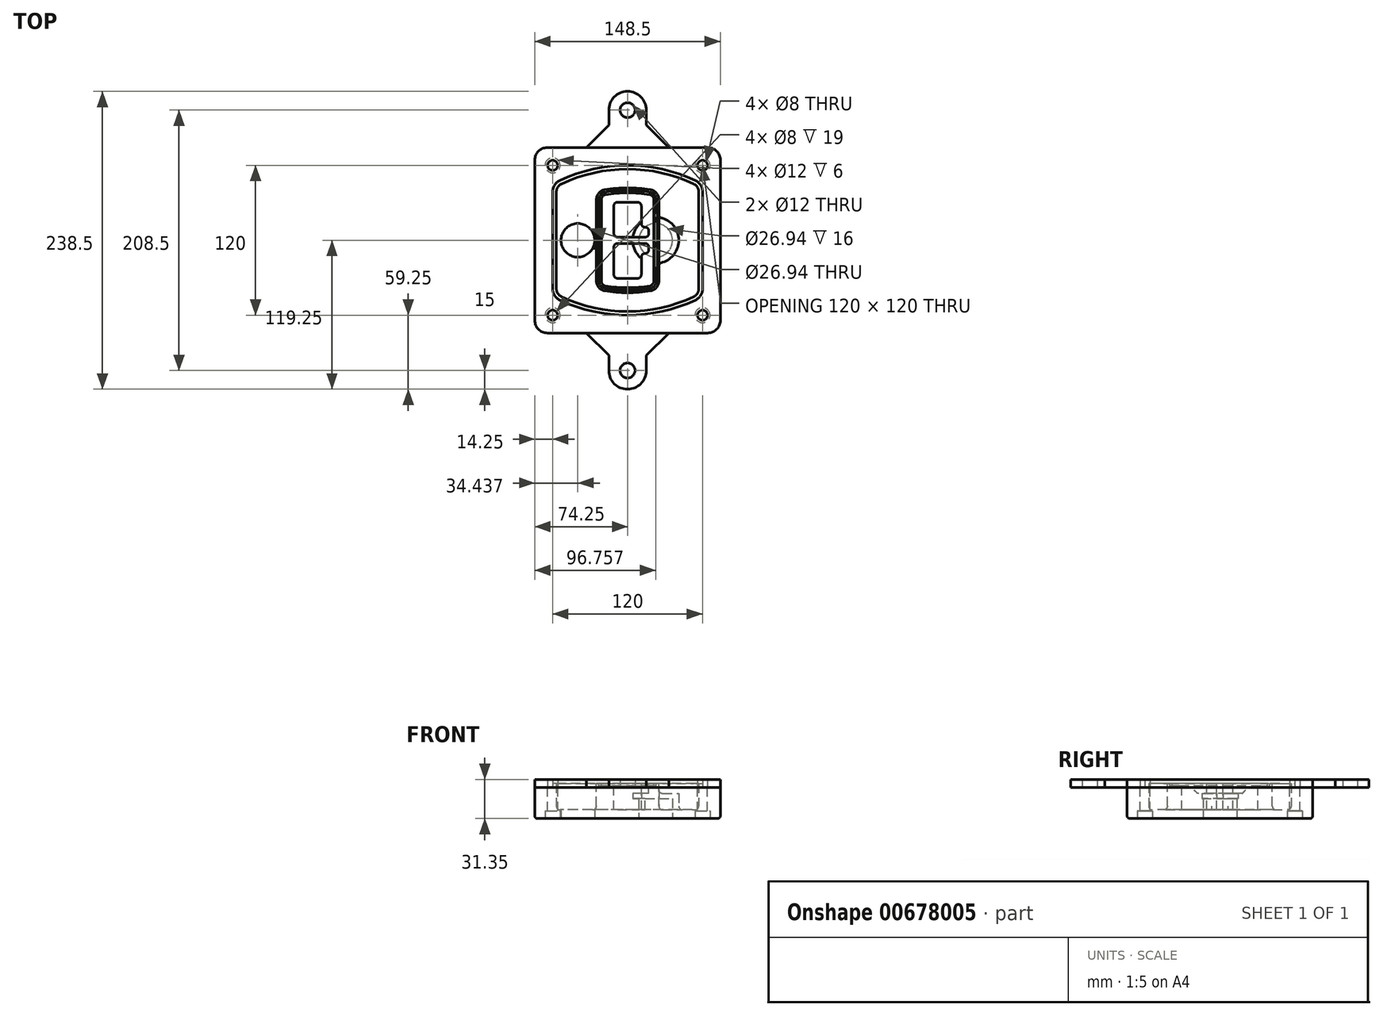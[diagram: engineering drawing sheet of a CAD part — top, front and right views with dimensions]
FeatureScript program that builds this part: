
annotation { "Feature Type Name" : "Feature", "Feature Type Description" : "" }
export const myFeature = defineFeature(function(context is Context, id is Id, definition is map)
    precondition{}
    {
        {
            var Q0;
            Q0=qCreatedBy(makeId("Top.planeOp"),FACE);
            var sketch = newSketch(context, id + "F0", { "sketchPlane" : qUnion([Q0])});
            skPoint(sketch, "E0.rect.middle", {"position": v(0, 0) * mm});
            skLineSegment(sketch, "E1.bottom", {"start": v(-64.25, -74.25) * mm, "end": v(64.25, -74.25) * mm});
            skLineSegment(sketch, "E1.top", {"start": v(-64.25, 74.25) * mm, "end": v(64.25, 74.25) * mm});
            skLineSegment(sketch, "E1.left", {"start": v(-74.25, -64.25) * mm, "end": v(-74.25, 64.25) * mm});
            skLineSegment(sketch, "E1.right", {"start": v(74.25, -64.25) * mm, "end": v(74.25, 64.25) * mm});
            skLineSegment(sketch, "E2", {"start": v(-74.25, 74.25) * mm, "end": v(74.25, -74.25) * mm, "construction": true});
            skLineSegment(sketch, "E3", {"start": v(74.25, 74.25) * mm, "end": v(-74.25, -74.25) * mm, "construction": true});
            skCircle(sketch, "E4", {"center": v(-60, 60) * mm, "radius": 4 * mm});
            skCircle(sketch, "E5", {"center": v(60, 60) * mm, "radius": 4 * mm});
            skCircle(sketch, "E6", {"center": v(60, -60) * mm, "radius": 4 * mm});
            skCircle(sketch, "E7", {"center": v(-60, -60) * mm, "radius": 4 * mm});
            skLineSegment(sketch, "E8", {"start": v(-60, 60) * mm, "end": v(60, 60) * mm, "construction": true});
            skLineSegment(sketch, "E9", {"start": v(60, 60) * mm, "end": v(60, -60) * mm, "construction": true});
            skLineSegment(sketch, "E10", {"start": v(60, -60) * mm, "end": v(-60, -60) * mm, "construction": true});
            skLineSegment(sketch, "E11", {"start": v(-60, -60) * mm, "end": v(-60, 60) * mm, "construction": true});
            skLineSegment(sketch, "E12", {"start": v(-60, 38.83) * mm, "end": v(-60, -38.83) * mm});
            skLineSegment(sketch, "E13", {"start": v(60, 38.83) * mm, "end": v(60, -38.83) * mm});
            skArc(sketch, "E14", {"start": v(54.26, 47.88) * mm, "mid": v(0, 60) * mm, "end": v(-54.26, 47.88) * mm});
            skArc(sketch, "E15", {"start": v(-54.26, -47.88) * mm, "mid": v(0, -60) * mm, "end": v(54.26, -47.88) * mm});
            skLineSegment(sketch, "E16", {"start": v(-60, 0) * mm, "end": v(60, 0) * mm, "construction": true});
            skPoint(sketch, "E17.visualSharp", {"position": v(-60, -45) * mm});
            skArc(sketch, "E17.filletArc", {"start": v(-60, -38.83) * mm, "mid": v(-58.44, -44.2) * mm, "end": v(-54.26, -47.88) * mm});
            skPoint(sketch, "E18.visualSharp", {"position": v(-60, 45) * mm});
            skArc(sketch, "E18.filletArc", {"start": v(-54.26, 47.88) * mm, "mid": v(-58.44, 44.2) * mm, "end": v(-60, 38.83) * mm});
            skPoint(sketch, "E19.visualSharp", {"position": v(60, 45) * mm});
            skArc(sketch, "E19.filletArc", {"start": v(60, 38.83) * mm, "mid": v(58.44, 44.2) * mm, "end": v(54.26, 47.88) * mm});
            skPoint(sketch, "E20.visualSharp", {"position": v(60, -45) * mm});
            skArc(sketch, "E20.filletArc", {"start": v(54.26, -47.88) * mm, "mid": v(58.44, -44.2) * mm, "end": v(60, -38.83) * mm});
            skPoint(sketch, "E21.visualSharp", {"position": v(-74.25, 74.25) * mm});
            skArc(sketch, "E21.filletArc", {"start": v(-64.25, 74.25) * mm, "mid": v(-71.32, 71.32) * mm, "end": v(-74.25, 64.25) * mm});
            skPoint(sketch, "E22.visualSharp", {"position": v(74.25, 74.25) * mm});
            skArc(sketch, "E22.filletArc", {"start": v(74.25, 64.25) * mm, "mid": v(71.32, 71.32) * mm, "end": v(64.25, 74.25) * mm});
            skPoint(sketch, "E23.visualSharp", {"position": v(74.25, -74.25) * mm});
            skArc(sketch, "E23.filletArc", {"start": v(64.25, -74.25) * mm, "mid": v(71.32, -71.32) * mm, "end": v(74.25, -64.25) * mm});
            skPoint(sketch, "E24.visualSharp", {"position": v(-74.25, -74.25) * mm});
            skArc(sketch, "E24.filletArc", {"start": v(-74.25, -64.25) * mm, "mid": v(-71.32, -71.32) * mm, "end": v(-64.25, -74.25) * mm});
            skArc(sketch, "E25.0", {"start": v(57, 38.83) * mm, "mid": v(55.9, 42.58) * mm, "end": v(52.98, 45.17) * mm});
            skLineSegment(sketch, "E25.1", {"start": v(57, 38.83) * mm, "end": v(57, -38.83) * mm});
            skArc(sketch, "E25.2", {"start": v(52.98, -45.17) * mm, "mid": v(55.9, -42.58) * mm, "end": v(57, -38.83) * mm});
            skArc(sketch, "E25.3", {"start": v(-52.98, -45.17) * mm, "mid": v(0, -57) * mm, "end": v(52.98, -45.17) * mm});
            skArc(sketch, "E25.4", {"start": v(-57, -38.83) * mm, "mid": v(-55.9, -42.58) * mm, "end": v(-52.98, -45.17) * mm});
            skArc(sketch, "E25.5", {"start": v(52.98, 45.17) * mm, "mid": v(0, 57) * mm, "end": v(-52.98, 45.17) * mm});
            skLineSegment(sketch, "E25.6", {"start": v(-57, 38.83) * mm, "end": v(-57, -38.83) * mm});
            skArc(sketch, "E25.7", {"start": v(-52.98, 45.17) * mm, "mid": v(-55.9, 42.58) * mm, "end": v(-57, 38.83) * mm});
            skArc(sketch, "E26.0", {"start": v(-55.96, 51.5) * mm, "mid": v(-61.82, 46.33) * mm, "end": v(-64, 38.83) * mm});
            skArc(sketch, "E26.1", {"start": v(55.96, 51.5) * mm, "mid": v(0, 64) * mm, "end": v(-55.96, 51.5) * mm});
            skArc(sketch, "E26.2", {"start": v(64, 38.83) * mm, "mid": v(61.82, 46.33) * mm, "end": v(55.96, 51.5) * mm});
            skLineSegment(sketch, "E26.3", {"start": v(64, 38.83) * mm, "end": v(64, -38.83) * mm});
            skArc(sketch, "E26.4", {"start": v(55.96, -51.5) * mm, "mid": v(61.82, -46.33) * mm, "end": v(64, -38.83) * mm});
            skLineSegment(sketch, "E26.5", {"start": v(-64, 38.83) * mm, "end": v(-64, -38.83) * mm});
            skArc(sketch, "E26.6", {"start": v(-55.96, -51.5) * mm, "mid": v(0, -64) * mm, "end": v(55.96, -51.5) * mm});
            skArc(sketch, "E26.7", {"start": v(-64, -38.83) * mm, "mid": v(-61.82, -46.33) * mm, "end": v(-55.96, -51.5) * mm});
            skSolve(sketch);
        }
        {
            var Q0;
            Q0=makeQuery(id+"F0.imprint","IMPRINT",FACE,{"disambiguationData":[TD([[makeQuery(id+"F0.imprint","IMPRINT",EDGE,{"derivedFrom":sQuery(id+"F0.wireOp",EDGE,"E1.bottom")}),1.0]])]});
            var Q1;
            Q1=makeQuery(id+"F0.imprint","IMPRINT",FACE,{"disambiguationData":[TD([[makeQuery(id+"F0.imprint","IMPRINT",EDGE,{"derivedFrom":sQuery(id+"F0.wireOp",EDGE,"E12")}),1.0]])]});
            var Q2;
            Q2=makeQuery(id+"F0.imprint","IMPRINT",FACE,{"disambiguationData":[TD([[makeQuery(id+"F0.imprint","IMPRINT",EDGE,{"derivedFrom":sQuery(id+"F0.wireOp",EDGE,"E25.0")}),1.0]])]});
            var Q3;
            Q3=makeQuery(id+"F0.imprint","IMPRINT",FACE,{"disambiguationData":[TD([[makeQuery(id+"F0.imprint","IMPRINT",EDGE,{"derivedFrom":sQuery(id+"F0.wireOp",EDGE,"E12")}),-1.0]])]});
            extrude(context, id + "F1", {"entities" : qUnion([Q0, Q1, Q2, Q3]), "oppositeDirection" : true, "depth" : 25 * mm});
        }
        {
            var Q0;
            Q0=makeQuery(id+"F0.imprint","IMPRINT",FACE,{"disambiguationData":[TD([[makeQuery(id+"F0.imprint","IMPRINT",EDGE,{"derivedFrom":sQuery(id+"F0.wireOp",EDGE,"E12")}),1.0]])]});
            extrude(context, id + "F2", {"entities" : qUnion([Q0]), "operationType" : NewBodyOperationType.ADD, "depth" : 3 * mm});
        }
        {
            var Q0;
            Q0=makeQuery(id+"F0.imprint","IMPRINT",FACE,{"disambiguationData":[TD([[makeQuery(id+"F0.imprint","IMPRINT",EDGE,{"derivedFrom":sQuery(id+"F0.wireOp",EDGE,"E25.0")}),1.0]])]});
            extrude(context, id + "F3", {"entities" : qUnion([Q0]), "operationType" : NewBodyOperationType.REMOVE, "oppositeDirection" : true, "depth" : 18 * mm});
        }
        {
            var Q0;
            Q0=makeQuery(id+"F2.opExtrude","CAP_FACE",FACE,{"disambiguationData":[OSD([sQuery(id+"F0.wireOp",EDGE,"E12"),sQuery(id+"F0.wireOp",EDGE,"E13"),sQuery(id+"F0.wireOp",EDGE,"E14"),sQuery(id+"F0.wireOp",EDGE,"E15"),sQuery(id+"F0.wireOp",EDGE,"E17.filletArc"),sQuery(id+"F0.wireOp",EDGE,"E18.filletArc"),sQuery(id+"F0.wireOp",EDGE,"E19.filletArc"),sQuery(id+"F0.wireOp",EDGE,"E20.filletArc"),sQuery(id+"F0.wireOp",EDGE,"E25.0"),sQuery(id+"F0.wireOp",EDGE,"E25.1"),sQuery(id+"F0.wireOp",EDGE,"E25.2"),sQuery(id+"F0.wireOp",EDGE,"E25.3"),sQuery(id+"F0.wireOp",EDGE,"E25.4"),sQuery(id+"F0.wireOp",EDGE,"E25.5"),sQuery(id+"F0.wireOp",EDGE,"E25.6"),sQuery(id+"F0.wireOp",EDGE,"E25.7")])],"isStart":false});
            var sketch = newSketch(context, id + "F4", { "sketchPlane" : qUnion([Q0])});
            skArc(sketch, "E27.0", {"start": v(-18.34, -40.45) * mm, "mid": v(0, -42) * mm, "end": v(18.34, -40.45) * mm});
            skArc(sketch, "E28.0", {"start": v(18.34, 40.45) * mm, "mid": v(0, 42) * mm, "end": v(-18.34, 40.45) * mm});
            skLineSegment(sketch, "E29", {"start": v(-25, 32.57) * mm, "end": v(-25, -32.57) * mm});
            skLineSegment(sketch, "E30", {"start": v(25, 32.57) * mm, "end": v(25, -32.57) * mm});
            skLineSegment(sketch, "E31", {"start": v(-25, 39.1) * mm, "end": v(25, 39.1) * mm, "construction": true});
            skLineSegment(sketch, "E32", {"start": v(-25, -39.1) * mm, "end": v(25, -39.1) * mm, "construction": true});
            skPoint(sketch, "E33.visualSharp", {"position": v(-25, 39.1) * mm});
            skArc(sketch, "E33.filletArc", {"start": v(-18.34, 40.45) * mm, "mid": v(-23.11, 37.73) * mm, "end": v(-25, 32.57) * mm});
            skPoint(sketch, "E34.visualSharp", {"position": v(25, 39.1) * mm});
            skArc(sketch, "E34.filletArc", {"start": v(25, 32.57) * mm, "mid": v(23.11, 37.73) * mm, "end": v(18.34, 40.45) * mm});
            skPoint(sketch, "E35.visualSharp", {"position": v(25, -39.1) * mm});
            skArc(sketch, "E35.filletArc", {"start": v(18.34, -40.45) * mm, "mid": v(23.11, -37.73) * mm, "end": v(25, -32.57) * mm});
            skPoint(sketch, "E36.visualSharp", {"position": v(-25, -39.1) * mm});
            skArc(sketch, "E36.filletArc", {"start": v(-25, -32.57) * mm, "mid": v(-23.11, -37.73) * mm, "end": v(-18.34, -40.45) * mm});
            skArc(sketch, "E37.0", {"start": v(52.98, 45.17) * mm, "mid": v(0, 57) * mm, "end": v(-52.98, 45.17) * mm});
            skArc(sketch, "E37.1", {"start": v(-52.98, 45.17) * mm, "mid": v(-55.9, 42.58) * mm, "end": v(-57, 38.83) * mm});
            skLineSegment(sketch, "E37.2", {"start": v(-57, 38.83) * mm, "end": v(-57, -38.83) * mm});
            skArc(sketch, "E37.3", {"start": v(-57, -38.83) * mm, "mid": v(-55.9, -42.58) * mm, "end": v(-52.98, -45.17) * mm});
            skArc(sketch, "E37.4", {"start": v(-52.98, -45.17) * mm, "mid": v(0, -57) * mm, "end": v(52.98, -45.17) * mm});
            skArc(sketch, "E37.5", {"start": v(52.98, -45.17) * mm, "mid": v(55.9, -42.58) * mm, "end": v(57, -38.83) * mm});
            skLineSegment(sketch, "E37.6", {"start": v(57, 38.83) * mm, "end": v(57, -38.83) * mm});
            skArc(sketch, "E37.7", {"start": v(57, 38.83) * mm, "mid": v(55.9, 42.58) * mm, "end": v(52.98, 45.17) * mm});
            skLineSegment(sketch, "E38.0", {"start": v(23, 32.57) * mm, "end": v(23, -32.57) * mm});
            skArc(sketch, "E38.1", {"start": v(18, -38.48) * mm, "mid": v(21.58, -36.44) * mm, "end": v(23, -32.57) * mm});
            skArc(sketch, "E38.2", {"start": v(-18, -38.48) * mm, "mid": v(0, -40) * mm, "end": v(18, -38.48) * mm});
            skArc(sketch, "E38.3", {"start": v(-23, -32.57) * mm, "mid": v(-21.58, -36.44) * mm, "end": v(-18, -38.48) * mm});
            skLineSegment(sketch, "E38.4", {"start": v(-23, 32.57) * mm, "end": v(-23, -32.57) * mm});
            skArc(sketch, "E38.5", {"start": v(23, 32.57) * mm, "mid": v(21.58, 36.44) * mm, "end": v(18, 38.48) * mm});
            skArc(sketch, "E38.6", {"start": v(-18, 38.48) * mm, "mid": v(-21.58, 36.44) * mm, "end": v(-23, 32.57) * mm});
            skArc(sketch, "E38.7", {"start": v(18, 38.48) * mm, "mid": v(0, 40) * mm, "end": v(-18, 38.48) * mm});
            skArc(sketch, "E39.0", {"start": v(21, 32.57) * mm, "mid": v(20.06, 35.15) * mm, "end": v(17.67, 36.5) * mm});
            skLineSegment(sketch, "E39.1", {"start": v(21, 32.57) * mm, "end": v(21, -32.57) * mm});
            skArc(sketch, "E39.2", {"start": v(17.67, -36.5) * mm, "mid": v(20.06, -35.15) * mm, "end": v(21, -32.57) * mm});
            skArc(sketch, "E39.3", {"start": v(-17.67, -36.5) * mm, "mid": v(0, -38) * mm, "end": v(17.67, -36.5) * mm});
            skArc(sketch, "E39.4", {"start": v(-21, -32.57) * mm, "mid": v(-20.06, -35.15) * mm, "end": v(-17.67, -36.5) * mm});
            skArc(sketch, "E39.5", {"start": v(17.67, 36.5) * mm, "mid": v(0, 38) * mm, "end": v(-17.67, 36.5) * mm});
            skLineSegment(sketch, "E39.6", {"start": v(-21, 32.57) * mm, "end": v(-21, -32.57) * mm});
            skArc(sketch, "E39.7", {"start": v(-17.67, 36.5) * mm, "mid": v(-20.06, 35.15) * mm, "end": v(-21, 32.57) * mm});
            skLineSegment(sketch, "E40", {"start": v(-25, 0) * mm, "end": v(25, 0) * mm, "construction": true});
            skLineSegment(sketch, "E41", {"start": v(-11, 5.5) * mm, "end": v(-11, 27.5) * mm});
            skLineSegment(sketch, "E42", {"start": v(-8, 30.5) * mm, "end": v(8, 30.5) * mm});
            skLineSegment(sketch, "E43", {"start": v(11, 27.5) * mm, "end": v(11, 13.5) * mm});
            skLineSegment(sketch, "E44", {"start": v(14, 10.5) * mm, "end": v(14, 10.5) * mm});
            skLineSegment(sketch, "E45", {"start": v(17, 7.5) * mm, "end": v(17, 5.5) * mm});
            skLineSegment(sketch, "E46", {"start": v(14, 2.5) * mm, "end": v(-8, 2.5) * mm});
            skPoint(sketch, "E47.visualSharp", {"position": v(-11, 30.5) * mm});
            skArc(sketch, "E47.filletArc", {"start": v(-8, 30.5) * mm, "mid": v(-10.12, 29.62) * mm, "end": v(-11, 27.5) * mm});
            skPoint(sketch, "E48.visualSharp", {"position": v(11, 30.5) * mm});
            skArc(sketch, "E48.filletArc", {"start": v(11, 27.5) * mm, "mid": v(10.12, 29.62) * mm, "end": v(8, 30.5) * mm});
            skPoint(sketch, "E49.visualSharp", {"position": v(11, 10.5) * mm});
            skArc(sketch, "E49.filletArc", {"start": v(11, 13.5) * mm, "mid": v(11.88, 11.38) * mm, "end": v(14, 10.5) * mm});
            skPoint(sketch, "E50.visualSharp", {"position": v(17, 10.5) * mm});
            skArc(sketch, "E50.filletArc", {"start": v(17, 7.5) * mm, "mid": v(16.12, 9.62) * mm, "end": v(14, 10.5) * mm});
            skPoint(sketch, "E51.visualSharp", {"position": v(17, 2.5) * mm});
            skArc(sketch, "E51.filletArc", {"start": v(14, 2.5) * mm, "mid": v(16.12, 3.38) * mm, "end": v(17, 5.5) * mm});
            skPoint(sketch, "E52.visualSharp", {"position": v(-11, 2.5) * mm});
            skArc(sketch, "E52.filletArc", {"start": v(-11, 5.5) * mm, "mid": v(-10.12, 3.38) * mm, "end": v(-8, 2.5) * mm});
            skLineSegment(sketch, "E53.0.MirrorCS", {"start": v(14, -2.5) * mm, "end": v(-8, -2.5) * mm});
            skArc(sketch, "E54.0.MirrorCS", {"start": v(-11, -5.5) * mm, "mid": v(-10.12, -3.38) * mm, "end": v(-8, -2.5) * mm});
            skLineSegment(sketch, "E55.0.MirrorCS", {"start": v(-11, -5.5) * mm, "end": v(-11, -27.5) * mm});
            skArc(sketch, "E56.0.MirrorCS", {"start": v(-8, -30.5) * mm, "mid": v(-10.12, -29.62) * mm, "end": v(-11, -27.5) * mm});
            skLineSegment(sketch, "E57.0.MirrorCS", {"start": v(-8, -30.5) * mm, "end": v(8, -30.5) * mm});
            skArc(sketch, "E58.0.MirrorCS", {"start": v(11, -27.5) * mm, "mid": v(10.12, -29.62) * mm, "end": v(8, -30.5) * mm});
            skLineSegment(sketch, "E59.0.MirrorCS", {"start": v(11, -27.5) * mm, "end": v(11, -13.5) * mm});
            skArc(sketch, "E60.0.MirrorCS", {"start": v(11, -13.5) * mm, "mid": v(11.88, -11.38) * mm, "end": v(14, -10.5) * mm});
            skArc(sketch, "E61.0.MirrorCS", {"start": v(17, -7.5) * mm, "mid": v(16.12, -9.62) * mm, "end": v(14, -10.5) * mm});
            skLineSegment(sketch, "E62.0.MirrorCS", {"start": v(17, -7.5) * mm, "end": v(17, -5.5) * mm});
            skArc(sketch, "E63.0.MirrorCS", {"start": v(14, -2.5) * mm, "mid": v(16.12, -3.38) * mm, "end": v(17, -5.5) * mm});
            skSolve(sketch);
        }
        {
            var Q0;
            Q0=makeQuery(id+"F4.imprint","IMPRINT",FACE,{"disambiguationData":[TD([[makeQuery(id+"F4.imprint","IMPRINT",EDGE,{"derivedFrom":sQuery(id+"F4.wireOp",EDGE,"E27.0")}),1.0]])]});
            var Q1;
            Q1=makeQuery(id+"F4.imprint","IMPRINT",FACE,{"disambiguationData":[TD([[makeQuery(id+"F4.imprint","IMPRINT",EDGE,{"derivedFrom":sQuery(id+"F4.wireOp",EDGE,"E38.0")}),-1.0]])]});
            var Q2;
            Q2=makeQuery(id+"F4.imprint","IMPRINT",FACE,{"disambiguationData":[TD([[makeQuery(id+"F4.imprint","IMPRINT",EDGE,{"derivedFrom":sQuery(id+"F4.wireOp",EDGE,"E39.0")}),1.0]])]});
            extrude(context, id + "F5", {"entities" : qUnion([Q0, Q1, Q2]), "operationType" : NewBodyOperationType.ADD, "endBound" : BoundingType.UP_TO_NEXT, "oppositeDirection" : true, "depth" : 25 * mm});
        }
        {
            var Q0;
            Q0=makeQuery(id+"F4.imprint","IMPRINT",FACE,{"disambiguationData":[TD([[makeQuery(id+"F4.imprint","IMPRINT",EDGE,{"derivedFrom":sQuery(id+"F4.wireOp",EDGE,"E38.0")}),-1.0]])]});
            extrude(context, id + "F6", {"entities" : qUnion([Q0]), "operationType" : NewBodyOperationType.REMOVE, "oppositeDirection" : true, "depth" : 2 * mm});
        }
        {
            var Q0;
            Q0=makeQuery(id+"F1.opExtrude","CAP_FACE",FACE,{"disambiguationData":[OSD([sQuery(id+"F0.wireOp",EDGE,"E1.bottom"),sQuery(id+"F0.wireOp",EDGE,"E1.top"),sQuery(id+"F0.wireOp",EDGE,"E1.left"),sQuery(id+"F0.wireOp",EDGE,"E1.right"),sQuery(id+"F0.wireOp",EDGE,"E4"),sQuery(id+"F0.wireOp",EDGE,"E5"),sQuery(id+"F0.wireOp",EDGE,"E6"),sQuery(id+"F0.wireOp",EDGE,"E7"),sQuery(id+"F0.wireOp",EDGE,"E21.filletArc"),sQuery(id+"F0.wireOp",EDGE,"E22.filletArc"),sQuery(id+"F0.wireOp",EDGE,"E23.filletArc"),sQuery(id+"F0.wireOp",EDGE,"E24.filletArc")])],"isStart":false});
            var sketch = newSketch(context, id + "F7", { "sketchPlane" : qUnion([Q0])});
            skCircle(sketch, "E64", {"center": v(22.5, 0) * mm, "radius": 13.47 * mm});
            skCircle(sketch, "E65", {"center": v(-39.81, 0) * mm, "radius": 13.47 * mm});
            skLineSegment(sketch, "E66", {"start": v(74.25, 0) * mm, "end": v(-74.25, 0) * mm});
            skCircle(sketch, "E67", {"center": v(22.5, 0) * mm, "radius": 18.47 * mm});
            skCircle(sketch, "E68", {"center": v(60, -60) * mm, "radius": 6 * mm});
            skCircle(sketch, "E69", {"center": v(-60, -60) * mm, "radius": 6 * mm});
            skCircle(sketch, "E70", {"center": v(-60, 60) * mm, "radius": 6 * mm});
            skCircle(sketch, "E71", {"center": v(60, 60) * mm, "radius": 6 * mm});
            skSolve(sketch);
        }
        {
            var Q0;
            {var subQ1=sQuery(id+"F7.wireOp",EDGE,"E66");var subQ4=sQuery(id+"F7.wireOp",EDGE,"E64");var subQ6=makeQuery(id+"F7.imprint","INTERSECT",VERTEX,{"disambiguationData":[OD(0.0)],"derivedFrom":[subQ4,subQ1]});Q0=makeQuery(id+"F7.imprint","IMPRINT",FACE,{"disambiguationData":[TD([[makeQuery(id+"F7.imprint","IMPRINT",EDGE,{"disambiguationData":[TD([[subQ6,-1.0]])],"derivedFrom":subQ4}),-1.0]])]});}
            var Q1;
            {var subQ0=sQuery(id+"F7.wireOp",EDGE,"E66");var subQ1=sQuery(id+"F7.wireOp",EDGE,"E64");var subQ3=makeQuery(id+"F7.imprint","INTERSECT",VERTEX,{"disambiguationData":[OD(0.0)],"derivedFrom":[subQ1,subQ0]});Q1=makeQuery(id+"F7.imprint","IMPRINT",FACE,{"disambiguationData":[TD([[makeQuery(id+"F7.imprint","IMPRINT",EDGE,{"disambiguationData":[TD([[subQ3,-1.0]])],"derivedFrom":subQ1}),1.0]])]});}
            var Q2;
            {var subQ0=sQuery(id+"F7.wireOp",EDGE,"E66");var subQ1=sQuery(id+"F7.wireOp",EDGE,"E64");var subQ3=makeQuery(id+"F7.imprint","INTERSECT",VERTEX,{"disambiguationData":[OD(0.0)],"derivedFrom":[subQ1,subQ0]});Q2=makeQuery(id+"F7.imprint","IMPRINT",FACE,{"disambiguationData":[TD([[makeQuery(id+"F7.imprint","IMPRINT",EDGE,{"disambiguationData":[TD([[subQ3,1.0]])],"derivedFrom":subQ1}),1.0]])]});}
            var Q3;
            {var subQ1=sQuery(id+"F7.wireOp",EDGE,"E66");var subQ4=sQuery(id+"F7.wireOp",EDGE,"E64");var subQ6=makeQuery(id+"F7.imprint","INTERSECT",VERTEX,{"disambiguationData":[OD(0.0)],"derivedFrom":[subQ4,subQ1]});Q3=makeQuery(id+"F7.imprint","IMPRINT",FACE,{"disambiguationData":[TD([[makeQuery(id+"F7.imprint","IMPRINT",EDGE,{"disambiguationData":[TD([[subQ6,1.0]])],"derivedFrom":subQ4}),-1.0]])]});}
            extrude(context, id + "F8", {"entities" : qUnion([Q0, Q1, Q2, Q3]), "operationType" : NewBodyOperationType.ADD, "oppositeDirection" : true, "depth" : 20 * mm});
        }
        {
            var Q0;
            {var subQ0=sQuery(id+"F7.wireOp",EDGE,"E66");var subQ1=sQuery(id+"F7.wireOp",EDGE,"E64");var subQ3=makeQuery(id+"F7.imprint","INTERSECT",VERTEX,{"disambiguationData":[OD(0.0)],"derivedFrom":[subQ1,subQ0]});Q0=makeQuery(id+"F7.imprint","IMPRINT",FACE,{"disambiguationData":[TD([[makeQuery(id+"F7.imprint","IMPRINT",EDGE,{"disambiguationData":[TD([[subQ3,-1.0]])],"derivedFrom":subQ1}),1.0]])]});}
            var Q1;
            {var subQ0=sQuery(id+"F7.wireOp",EDGE,"E66");var subQ1=sQuery(id+"F7.wireOp",EDGE,"E64");var subQ3=makeQuery(id+"F7.imprint","INTERSECT",VERTEX,{"disambiguationData":[OD(0.0)],"derivedFrom":[subQ1,subQ0]});Q1=makeQuery(id+"F7.imprint","IMPRINT",FACE,{"disambiguationData":[TD([[makeQuery(id+"F7.imprint","IMPRINT",EDGE,{"disambiguationData":[TD([[subQ3,1.0]])],"derivedFrom":subQ1}),1.0]])]});}
            extrude(context, id + "F9", {"entities" : qUnion([Q0, Q1]), "operationType" : NewBodyOperationType.REMOVE, "oppositeDirection" : true, "depth" : 16 * mm});
        }
        {
            var Q0;
            {var subQ0=sQuery(id+"F7.wireOp",EDGE,"E66");var subQ1=sQuery(id+"F7.wireOp",EDGE,"E65");var subQ3=makeQuery(id+"F7.imprint","INTERSECT",VERTEX,{"disambiguationData":[OD(0.0)],"derivedFrom":[subQ1,subQ0]});Q0=makeQuery(id+"F7.imprint","IMPRINT",FACE,{"disambiguationData":[TD([[makeQuery(id+"F7.imprint","IMPRINT",EDGE,{"disambiguationData":[TD([[subQ3,-1.0]])],"derivedFrom":subQ1}),1.0]])]});}
            var Q1;
            {var subQ0=sQuery(id+"F7.wireOp",EDGE,"E66");var subQ1=sQuery(id+"F7.wireOp",EDGE,"E65");var subQ3=makeQuery(id+"F7.imprint","INTERSECT",VERTEX,{"disambiguationData":[OD(0.0)],"derivedFrom":[subQ1,subQ0]});Q1=makeQuery(id+"F7.imprint","IMPRINT",FACE,{"disambiguationData":[TD([[makeQuery(id+"F7.imprint","IMPRINT",EDGE,{"disambiguationData":[TD([[subQ3,1.0]])],"derivedFrom":subQ1}),1.0]])]});}
            extrude(context, id + "F10", {"entities" : qUnion([Q0, Q1]), "operationType" : NewBodyOperationType.REMOVE, "oppositeDirection" : true, "depth" : 25 * mm});
        }
        {
            var Q0;
            Q0=makeQuery(id+"F7.imprint","IMPRINT",FACE,{"disambiguationData":[TD([[makeQuery(id+"F7.imprint","IMPRINT",EDGE,{"derivedFrom":sQuery(id+"F7.wireOp",EDGE,"E68")}),1.0]])]});
            var Q1;
            Q1=makeQuery(id+"F7.imprint","IMPRINT",FACE,{"disambiguationData":[TD([[makeQuery(id+"F7.imprint","IMPRINT",EDGE,{"derivedFrom":makeQuery(id+"F1.opExtrude","CAP_EDGE",EDGE,{"disambiguationData":[OSD([sQuery(id+"F0.wireOp",EDGE,"E5")])],"isStart":false})}),-1.0]])]});
            var Q2;
            Q2=makeQuery(id+"F7.imprint","IMPRINT",FACE,{"disambiguationData":[TD([[makeQuery(id+"F7.imprint","IMPRINT",EDGE,{"derivedFrom":sQuery(id+"F7.wireOp",EDGE,"E69")}),1.0]])]});
            var Q3;
            Q3=makeQuery(id+"F7.imprint","IMPRINT",FACE,{"disambiguationData":[TD([[makeQuery(id+"F7.imprint","IMPRINT",EDGE,{"derivedFrom":makeQuery(id+"F1.opExtrude","CAP_EDGE",EDGE,{"disambiguationData":[OSD([sQuery(id+"F0.wireOp",EDGE,"E4")])],"isStart":false})}),-1.0]])]});
            var Q4;
            Q4=makeQuery(id+"F7.imprint","IMPRINT",FACE,{"disambiguationData":[TD([[makeQuery(id+"F7.imprint","IMPRINT",EDGE,{"derivedFrom":sQuery(id+"F7.wireOp",EDGE,"E70")}),1.0]])]});
            var Q5;
            Q5=makeQuery(id+"F7.imprint","IMPRINT",FACE,{"disambiguationData":[TD([[makeQuery(id+"F7.imprint","IMPRINT",EDGE,{"derivedFrom":makeQuery(id+"F1.opExtrude","CAP_EDGE",EDGE,{"disambiguationData":[OSD([sQuery(id+"F0.wireOp",EDGE,"E7")])],"isStart":false})}),-1.0]])]});
            var Q6;
            Q6=makeQuery(id+"F7.imprint","IMPRINT",FACE,{"disambiguationData":[TD([[makeQuery(id+"F7.imprint","IMPRINT",EDGE,{"derivedFrom":sQuery(id+"F7.wireOp",EDGE,"E71")}),1.0]])]});
            var Q7;
            Q7=makeQuery(id+"F7.imprint","IMPRINT",FACE,{"disambiguationData":[TD([[makeQuery(id+"F7.imprint","IMPRINT",EDGE,{"derivedFrom":makeQuery(id+"F1.opExtrude","CAP_EDGE",EDGE,{"disambiguationData":[OSD([sQuery(id+"F0.wireOp",EDGE,"E6")])],"isStart":false})}),-1.0]])]});
            extrude(context, id + "F11", {"entities" : qUnion([Q0, Q1, Q2, Q3, Q4, Q5, Q6, Q7]), "operationType" : NewBodyOperationType.REMOVE, "oppositeDirection" : true, "depth" : 6 * mm});
        }
        {
            var Q0;
            Q0=makeQuery(id+"F9.boolean.opBoolean","COPY",FACE,{"derivedFrom":makeQuery(id+"F9.opExtrude","CAP_FACE",FACE,{"disambiguationData":[OSD([sQuery(id+"F7.wireOp",EDGE,"E64")])],"isStart":false})});
            var sketch = newSketch(context, id + "F12", { "sketchPlane" : qUnion([Q0])});
            skArc(sketch, "E72.0", {"start": v(11, 14.45) * mm, "mid": v(6.45, 9.13) * mm, "end": v(4.2, 2.5) * mm});
            skArc(sketch, "E72.1", {"start": v(4.2, -2.5) * mm, "mid": v(6.45, -9.13) * mm, "end": v(11, -14.45) * mm});
            skLineSegment(sketch, "E73", {"start": v(4.2, -2.5) * mm, "end": v(14, -2.5) * mm});
            skLineSegment(sketch, "E74.0", {"start": v(14, 2.5) * mm, "end": v(4.2, 2.5) * mm});
            skArc(sketch, "E74.1", {"start": v(14, 2.5) * mm, "mid": v(16.12, 3.38) * mm, "end": v(17, 5.5) * mm});
            skLineSegment(sketch, "E74.2", {"start": v(17, 7.5) * mm, "end": v(17, 5.5) * mm});
            skArc(sketch, "E74.3", {"start": v(17, 7.5) * mm, "mid": v(16.12, 9.62) * mm, "end": v(14, 10.5) * mm});
            skArc(sketch, "E74.4", {"start": v(11, 13.5) * mm, "mid": v(11.88, 11.38) * mm, "end": v(14, 10.5) * mm});
            skLineSegment(sketch, "E74.5", {"start": v(11, 14.45) * mm, "end": v(11, 13.5) * mm});
            skLineSegment(sketch, "E74.7", {"start": v(14, -2.5) * mm, "end": v(4.2, -2.5) * mm});
            skArc(sketch, "E74.8", {"start": v(14, -2.5) * mm, "mid": v(16.12, -3.38) * mm, "end": v(17, -5.5) * mm});
            skLineSegment(sketch, "E74.9", {"start": v(17, -7.5) * mm, "end": v(17, -5.5) * mm});
            skArc(sketch, "E74.10", {"start": v(17, -7.5) * mm, "mid": v(16.12, -9.62) * mm, "end": v(14, -10.5) * mm});
            skArc(sketch, "E74.11", {"start": v(11, -13.5) * mm, "mid": v(11.88, -11.38) * mm, "end": v(14, -10.5) * mm});
            skLineSegment(sketch, "E74.12", {"start": v(11, -14.45) * mm, "end": v(11, -13.5) * mm});
            skPoint(sketch, "E75.orphan", {"position": v(11, -27.5) * mm});
            skPoint(sketch, "E76.orphan", {"position": v(-8, -2.5) * mm});
            skPoint(sketch, "E77.orphan", {"position": v(-8, 2.5) * mm});
            skPoint(sketch, "E78.orphan", {"position": v(11, 27.5) * mm});
            skSolve(sketch);
        }
        {
            var Q0;
            {var subQ7=sQuery(id+"F12.wireOp",EDGE,"E72.0");var subQ14=sQuery(id+"F12.wireOp",EDGE,"E72.1");var subQ16=sQuery(id+"F12.wireOp",EDGE,"E74.1");var subQ18=sQuery(id+"F12.wireOp",EDGE,"E74.8");Q0=qUnion([makeQuery(id+"F12.imprint","IMPRINT",FACE,{"disambiguationData":[TD([[makeQuery(id+"F12.imprint","IMPRINT",EDGE,{"derivedFrom":subQ7}),1.0]])]}),makeQuery(id+"F12.imprint","IMPRINT",FACE,{"disambiguationData":[TD([[makeQuery(id+"F12.imprint","IMPRINT",EDGE,{"derivedFrom":subQ14}),1.0]])]}),makeQuery(id+"F12.imprint","IMPRINT",FACE,{"disambiguationData":[TD([[makeQuery(id+"F12.imprint","IMPRINT",EDGE,{"derivedFrom":subQ16}),1.0]])]}),makeQuery(id+"F12.imprint","IMPRINT",FACE,{"disambiguationData":[TD([[makeQuery(id+"F12.imprint","IMPRINT",EDGE,{"derivedFrom":subQ18}),-1.0]])]})]);}
            var Q1;
            Q1=makeQuery(id+"F5.boolean.opBoolean","SPLIT",FACE,{"disambiguationData":[TD([makeQuery(id+"F5.opExtrude","SWEPT_FACE",FACE,{"disambiguationData":[OSD([sQuery(id+"F4.wireOp",EDGE,"E41")])]})])],"derivedFrom":makeQuery(id+"F3.boolean.opBoolean","COPY",FACE,{"derivedFrom":makeQuery(id+"F3.opExtrude","CAP_FACE",FACE,{"disambiguationData":[OSD([sQuery(id+"F0.wireOp",EDGE,"E25.0"),sQuery(id+"F0.wireOp",EDGE,"E25.1"),sQuery(id+"F0.wireOp",EDGE,"E25.2"),sQuery(id+"F0.wireOp",EDGE,"E25.3"),sQuery(id+"F0.wireOp",EDGE,"E25.4"),sQuery(id+"F0.wireOp",EDGE,"E25.5"),sQuery(id+"F0.wireOp",EDGE,"E25.6"),sQuery(id+"F0.wireOp",EDGE,"E25.7")])],"isStart":false})})});
            extrude(context, id + "F13", {"entities" : qUnion([Q0]), "operationType" : NewBodyOperationType.REMOVE, "endBound" : BoundingType.UP_TO_SURFACE, "endBoundEntityFace" : qUnion([Q1]), "depth" : 25 * mm});
        }
        {
            var Q0;
            Q0=makeQuery(id+"F3.boolean.opBoolean","COPY",EDGE,{"derivedFrom":makeQuery(id+"F3.opExtrude","CAP_EDGE",EDGE,{"disambiguationData":[OSD([sQuery(id+"F0.wireOp",EDGE,"E25.6")])],"isStart":false})});
            var Q1;
            Q1=makeQuery(id+"F8.boolean.opBoolean","INTERSECT",EDGE,{"derivedFrom":[makeQuery(id+"F5.opExtrude","SWEPT_FACE",FACE,{"disambiguationData":[OSD([sQuery(id+"F4.wireOp",EDGE,"E30")])]}),makeQuery(id+"F8.opExtrude","CAP_FACE",FACE,{"disambiguationData":[OSD([sQuery(id+"F7.wireOp",EDGE,"E67")])],"isStart":false})]});
            var Q2;
            Q2=makeQuery(id+"F8.boolean.opBoolean","INTERSECT",EDGE,{"disambiguationData":[OD(1.0)],"derivedFrom":[makeQuery(id+"F5.opExtrude","SWEPT_FACE",FACE,{"disambiguationData":[OSD([sQuery(id+"F4.wireOp",EDGE,"E30")])]}),makeQuery(id+"F8.opExtrude","SWEPT_FACE",FACE,{"disambiguationData":[OSD([sQuery(id+"F7.wireOp",EDGE,"E67")])]})]});
            var Q3;
            {var subQ0=sQuery(id+"F4.wireOp",EDGE,"E30");Q3=makeQuery(id+"F8.boolean.opBoolean","SPLIT",EDGE,{"disambiguationData":[TD([makeQuery(id+"F5.opExtrude","SWEPT_FACE",FACE,{"disambiguationData":[OSD([sQuery(id+"F4.wireOp",EDGE,"E35.filletArc")])]})])],"derivedFrom":makeQuery(id+"F5.opExtrude","CAP_EDGE",EDGE,{"disambiguationData":[OSD([subQ0])],"isStart":false})});}
            var Q4;
            {var subQ0=sQuery(id+"F0.wireOp",EDGE,"E25.7");var subQ1=sQuery(id+"F0.wireOp",EDGE,"E25.1");var subQ2=sQuery(id+"F0.wireOp",EDGE,"E25.6");var subQ3=sQuery(id+"F0.wireOp",EDGE,"E25.5");var subQ4=sQuery(id+"F0.wireOp",EDGE,"E25.4");var subQ5=sQuery(id+"F0.wireOp",EDGE,"E25.0");var subQ6=sQuery(id+"F0.wireOp",EDGE,"E25.2");var subQ7=sQuery(id+"F0.wireOp",EDGE,"E25.3");Q4=makeQuery(id+"F8.boolean.opBoolean","INTERSECT",EDGE,{"derivedFrom":[makeQuery(id+"F5.boolean.opBoolean","SPLIT",FACE,{"disambiguationData":[TD([makeQuery(id+"F2.opExtrude","SWEPT_FACE",FACE,{"disambiguationData":[OSD([subQ5])]})])],"derivedFrom":makeQuery(id+"F3.boolean.opBoolean","COPY",FACE,{"derivedFrom":makeQuery(id+"F3.opExtrude","CAP_FACE",FACE,{"disambiguationData":[OSD([subQ5,subQ1,subQ6,subQ7,subQ4,subQ3,subQ2,subQ0])],"isStart":false})})}),makeQuery(id+"F8.opExtrude","SWEPT_FACE",FACE,{"disambiguationData":[OSD([sQuery(id+"F7.wireOp",EDGE,"E67")])]})]});}
            var Q5;
            Q5=makeQuery(id+"F8.boolean.opBoolean","INTERSECT",EDGE,{"disambiguationData":[OD(0.0)],"derivedFrom":[makeQuery(id+"F5.opExtrude","SWEPT_FACE",FACE,{"disambiguationData":[OSD([sQuery(id+"F4.wireOp",EDGE,"E30")])]}),makeQuery(id+"F8.opExtrude","SWEPT_FACE",FACE,{"disambiguationData":[OSD([sQuery(id+"F7.wireOp",EDGE,"E67")])]})]});
            fillet(context, id + "F14", {"entities" : qUnion([Q0, Q1, Q2, Q3, Q4, Q5]), "radius" : 3 * mm, "tangentPropagation" : true, "allowEdgeOverflow" : false});
        }
        {
            var Q0;
            Q0=makeQuery(id+"F1.opExtrude","CAP_EDGE",EDGE,{"disambiguationData":[OSD([sQuery(id+"F0.wireOp",EDGE,"E1.bottom")])],"isStart":false});
            fillet(context, id + "F15", {"entities" : qUnion([Q0]), "radius" : 2 * mm, "tangentPropagation" : true, "allowEdgeOverflow" : false});
        }
        {
            var Q0;
            {var subQ0=sQuery(id+"F0.wireOp",EDGE,"E21.filletArc");var subQ1=sQuery(id+"F0.wireOp",EDGE,"E7");var subQ2=sQuery(id+"F0.wireOp",EDGE,"E6");var subQ3=sQuery(id+"F0.wireOp",EDGE,"E5");var subQ4=sQuery(id+"F0.wireOp",EDGE,"E4");var subQ5=sQuery(id+"F0.wireOp",EDGE,"E22.filletArc");var subQ6=sQuery(id+"F0.wireOp",EDGE,"E1.bottom");var subQ7=sQuery(id+"F0.wireOp",EDGE,"E1.right");var subQ8=sQuery(id+"F0.wireOp",EDGE,"E1.top");var subQ9=sQuery(id+"F0.wireOp",EDGE,"E1.left");var subQ10=sQuery(id+"F0.wireOp",EDGE,"E23.filletArc");var subQ11=sQuery(id+"F0.wireOp",EDGE,"E24.filletArc");Q0=makeQuery(id+"F2.boolean.opBoolean","SPLIT",FACE,{"disambiguationData":[TD([makeQuery(id+"F1.opExtrude","SWEPT_FACE",FACE,{"disambiguationData":[OSD([subQ6])]})])],"derivedFrom":makeQuery(id+"F1.opExtrude","CAP_FACE",FACE,{"disambiguationData":[OSD([subQ6,subQ8,subQ9,subQ7,subQ4,subQ3,subQ2,subQ1,subQ0,subQ5,subQ10,subQ11])],"isStart":true})});}
            var sketch = newSketch(context, id + "F16", { "sketchPlane" : qUnion([Q0])});
            skLineSegment(sketch, "E79", {"start": v(0, 74.25) * mm, "end": v(0, 104.25) * mm, "construction": true});
            skPoint(sketch, "E79.endSnap0", {"position": v(0, 74.25) * mm});
            skCircle(sketch, "E80", {"center": v(0, 104.25) * mm, "radius": 6 * mm});
            skArc(sketch, "E81", {"start": v(15, 104.25) * mm, "mid": v(0, 119.25) * mm, "end": v(-15, 104.25) * mm});
            skLineSegment(sketch, "E82", {"start": v(-15, 104.25) * mm, "end": v(-15, 92.25) * mm});
            skLineSegment(sketch, "E83", {"start": v(15, 104.25) * mm, "end": v(15, 92.25) * mm});
            skLineSegment(sketch, "E84", {"start": v(-33, 74.25) * mm, "end": v(-15, 92.25) * mm});
            skLineSegment(sketch, "E85", {"start": v(33, 74.25) * mm, "end": v(15, 92.25) * mm});
            skLineSegment(sketch, "E86", {"start": v(-74.25, 0) * mm, "end": v(74.25, 0) * mm, "construction": true});
            skLineSegment(sketch, "E87.MirrorCS", {"start": v(33, -74.25) * mm, "end": v(15, -92.25) * mm});
            skLineSegment(sketch, "E88.MirrorCS", {"start": v(15, -104.25) * mm, "end": v(15, -92.25) * mm});
            skArc(sketch, "E89.MirrorCS", {"start": v(15, -104.25) * mm, "mid": v(0, -119.25) * mm, "end": v(-15, -104.25) * mm});
            skLineSegment(sketch, "E90.MirrorCS", {"start": v(-15, -104.25) * mm, "end": v(-15, -92.25) * mm});
            skLineSegment(sketch, "E91.MirrorCS", {"start": v(-33, -74.25) * mm, "end": v(-15, -92.25) * mm});
            skCircle(sketch, "E92.MirrorC", {"center": v(0, -104.25) * mm, "radius": 6 * mm});
            skLineSegment(sketch, "E93.MirrorCS", {"start": v(0, -74.25) * mm, "end": v(0, -104.25) * mm, "construction": true});
            skSolve(sketch);
        }
        {
            var Q0;
            Q0=makeQuery(id+"F16.imprint","IMPRINT",FACE,{"disambiguationData":[TD([[makeQuery(id+"F16.imprint","IMPRINT",EDGE,{"derivedFrom":sQuery(id+"F16.wireOp",EDGE,"E80")}),-1.0]])]});
            var Q1;
            {var subQ0=sQuery(id+"F16.wireOp",EDGE,"E87.MirrorCS");Q1=makeQuery(id+"F16.imprint","IMPRINT",FACE,{"disambiguationData":[TD([[makeQuery(id+"F16.imprint","IMPRINT",EDGE,{"derivedFrom":subQ0}),-1.0]])]});}
            extrude(context, id + "F17", {"entities" : qUnion([Q0, Q1]), "depth" : 6.35 * mm, "offsetDistance" : 25.4 * mm});
        }
        {
            var Q0;
            {var subQ0=sQuery(id+"F0.wireOp",EDGE,"E21.filletArc");var subQ1=sQuery(id+"F0.wireOp",EDGE,"E7");var subQ2=sQuery(id+"F0.wireOp",EDGE,"E6");var subQ3=sQuery(id+"F0.wireOp",EDGE,"E5");var subQ4=sQuery(id+"F0.wireOp",EDGE,"E4");var subQ5=sQuery(id+"F0.wireOp",EDGE,"E22.filletArc");var subQ6=sQuery(id+"F0.wireOp",EDGE,"E1.bottom");var subQ7=sQuery(id+"F0.wireOp",EDGE,"E1.right");var subQ8=sQuery(id+"F0.wireOp",EDGE,"E1.top");var subQ9=sQuery(id+"F0.wireOp",EDGE,"E1.left");var subQ10=sQuery(id+"F0.wireOp",EDGE,"E23.filletArc");var subQ11=sQuery(id+"F0.wireOp",EDGE,"E24.filletArc");Q0=makeQuery(id+"F2.boolean.opBoolean","SPLIT",FACE,{"disambiguationData":[TD([makeQuery(id+"F1.opExtrude","SWEPT_FACE",FACE,{"disambiguationData":[OSD([subQ6])]})])],"derivedFrom":makeQuery(id+"F1.opExtrude","CAP_FACE",FACE,{"disambiguationData":[OSD([subQ6,subQ8,subQ9,subQ7,subQ4,subQ3,subQ2,subQ1,subQ0,subQ5,subQ10,subQ11])],"isStart":true})});}
            extrude(context, id + "F18", {"entities" : qUnion([Q0]), "depth" : 6.35 * mm, "offsetDistance" : 25.4 * mm});
        }
    });
